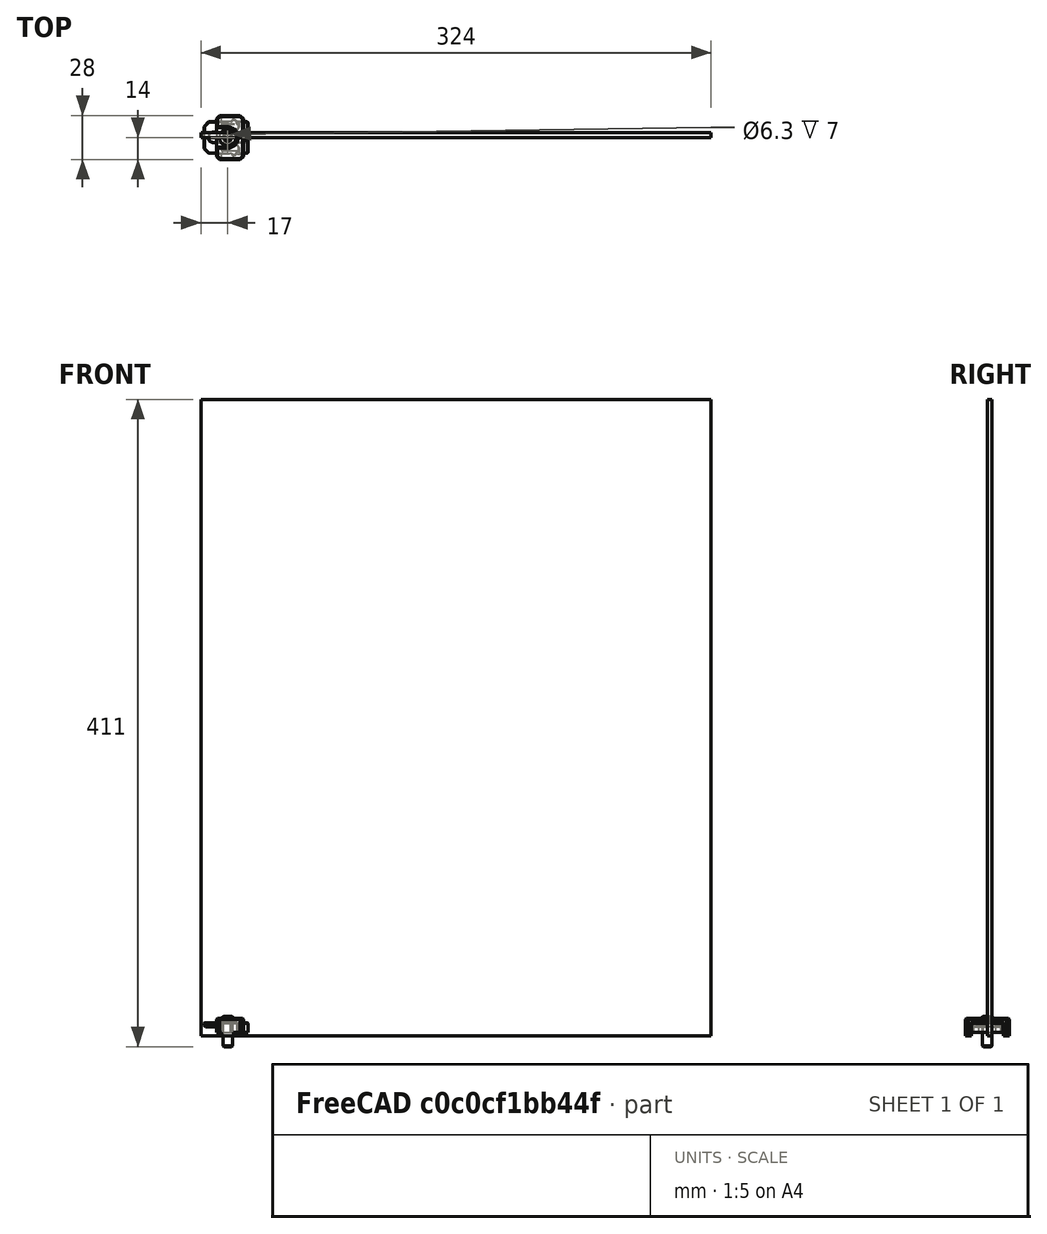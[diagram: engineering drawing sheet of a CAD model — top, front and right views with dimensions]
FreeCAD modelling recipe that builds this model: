
FCSTD DOCUMENT  (FreeCAD 0.19R24291 (Git))
Label: side-panell-assembly
License: Other
LicenseURL: GPL3
objects: Part::Feature×24, App::Part×13, Part::FeaturePython×12, Part::Box×1
note: 37 computed .brp shape members not serialized (recipe doc carries the construction recipe); baked Part::Feature solids carry a one-line shape summary decoded from their .brp

FEATURE [Part::Box] Box  label="panel-324x404x3mm"
  AttacherType = Attacher::AttachEngine3D
  Height = 404
  Length = 324
  Placement = pos=(-2,0,-2) rot=(0,0,1;0rad)
  Width = 3
FEATURE [Part::Feature] Chamfer008001013
  shape: bbox 28 x 22 x 6 mm, 82 faces (baked)
FEATURE [Part::Feature] Chamfer008002001001
  shape: bbox 17 x 28 x 11 mm, 53 faces (baked)
FEATURE [Part::FeaturePython] Screw  label="M6x16-Screw"  # Fasteners workbench fastener (typed FeaturePython)
  Placement = pos=(15,0,7) rot=(0,0,1;0rad)
  baseObject = -> Chamfer008002001001 [Edge135]
  diameter = 4
  invert = false
  length = 3
  lengthCustom = 16
  matchOuter = false
  offset = 0
  thread = false
  type = 40
FEATURE [App::Part] Part013  label="Panel-mounterr2-000"
  Group = -> [Chamfer008001013,Chamfer008002001001,Screw]
  Origin = -> Origin013
  Placement = pos=(39,3,5) rot=(-0.57735,-0.57735,0.57735;4.18879rad)
FEATURE [Part::Feature] Chamfer008002001002
  shape: bbox 28 x 22 x 6 mm, 82 faces (baked)
FEATURE [Part::Feature] Chamfer008002001003
  shape: bbox 17 x 28 x 11 mm, 53 faces (baked)
FEATURE [Part::FeaturePython] Screw024  label="M6x16-Screw001"  # Fasteners workbench fastener (typed FeaturePython)
  Placement = pos=(15,0,7) rot=(0,0,1;0rad)
  baseObject = -> Chamfer008002001003 [Edge135]
  diameter = 4
  invert = false
  length = 3
  lengthCustom = 16
  matchOuter = false
  offset = 0
  thread = false
  type = 40
FEATURE [App::Part] Part014  label="Panel-mounterr2-001"
  Group = -> [Chamfer008002001002,Chamfer008002001003,Screw024]
  Origin = -> Origin014
  Placement = pos=(160,3,5) rot=(-0.57735,-0.57735,0.57735;4.18879rad)
FEATURE [Part::Feature] Chamfer008002001004
  shape: bbox 28 x 22 x 6 mm, 82 faces (baked)
FEATURE [Part::Feature] Chamfer008002001005
  shape: bbox 17 x 28 x 11 mm, 53 faces (baked)
FEATURE [Part::FeaturePython] Screw025  label="M6x16-Screw002"  # Fasteners workbench fastener (typed FeaturePython)
  Placement = pos=(15,0,7) rot=(0,0,1;0rad)
  baseObject = -> Chamfer008002001005 [Edge135]
  diameter = 4
  invert = false
  length = 3
  lengthCustom = 16
  matchOuter = false
  offset = 0
  thread = false
  type = 40
FEATURE [App::Part] Part015  label="Panel-mounterr2-002"
  Group = -> [Chamfer008002001004,Chamfer008002001005,Screw025]
  Origin = -> Origin015
  Placement = pos=(280.5,3,5) rot=(-0.57735,-0.57735,0.57735;4.18879rad)
FEATURE [Part::Feature] Chamfer008002001006
  shape: bbox 28 x 22 x 6 mm, 82 faces (baked)
FEATURE [Part::Feature] Chamfer008002001007
  shape: bbox 17 x 28 x 11 mm, 53 faces (baked)
FEATURE [Part::FeaturePython] Screw026  label="M6x16-Screw003"  # Fasteners workbench fastener (typed FeaturePython)
  Placement = pos=(15,0,7) rot=(0,0,1;0rad)
  baseObject = -> Chamfer008002001007 [Edge135]
  diameter = 4
  invert = false
  length = 3
  lengthCustom = 16
  matchOuter = false
  offset = 0
  thread = false
  type = 40
FEATURE [App::Part] Part016  label="Panel-mounterr2-003"
  Group = -> [Chamfer008002001006,Chamfer008002001007,Screw026]
  Origin = -> Origin016
  Placement = pos=(315,3,39) rot=(-1,0,0;4.71239rad)
FEATURE [Part::Feature] Chamfer008002001008
  shape: bbox 17 x 28 x 11 mm, 53 faces (baked)
FEATURE [Part::FeaturePython] Screw027  label="M6x16-Screw004"  # Fasteners workbench fastener (typed FeaturePython)
  Placement = pos=(15,0,7) rot=(0,0,1;0rad)
  baseObject = -> Chamfer008002001008 [Edge135]
  diameter = 4
  invert = false
  length = 3
  lengthCustom = 16
  matchOuter = false
  offset = 0
  thread = false
  type = 40
FEATURE [Part::Feature] Chamfer008002001009
  shape: bbox 28 x 22 x 6 mm, 82 faces (baked)
FEATURE [App::Part] Part017  label="Panel-mounterr2-004"
  Group = -> [Chamfer008002001009,Chamfer008002001008,Screw027]
  Origin = -> Origin017
  Placement = pos=(315,3,190) rot=(-1,0,0;4.71239rad)
FEATURE [Part::Feature] Chamfer008002001010
  shape: bbox 17 x 28 x 11 mm, 53 faces (baked)
FEATURE [Part::FeaturePython] Screw028  label="M6x16-Screw005"  # Fasteners workbench fastener (typed FeaturePython)
  Placement = pos=(15,0,7) rot=(0,0,1;0rad)
  baseObject = -> Chamfer008002001010 [Edge135]
  diameter = 4
  invert = false
  length = 3
  lengthCustom = 16
  matchOuter = false
  offset = 0
  thread = false
  type = 40
FEATURE [Part::Feature] Chamfer008002001011
  shape: bbox 28 x 22 x 6 mm, 82 faces (baked)
FEATURE [App::Part] Part018  label="Panel-mounterr2-005"
  Group = -> [Chamfer008002001011,Chamfer008002001010,Screw028]
  Origin = -> Origin018
  Placement = pos=(315,3,361) rot=(-1,0,0;4.71239rad)
FEATURE [Part::FeaturePython] Screw029  label="M6x16-Screw006"  # Fasteners workbench fastener (typed FeaturePython)
  Placement = pos=(15,0,7) rot=(0,0,1;0rad)
  baseObject = -> Chamfer008002001012 [Edge135]
  diameter = 4
  invert = false
  length = 3
  lengthCustom = 16
  matchOuter = false
  offset = 0
  thread = false
  type = 40
FEATURE [Part::Feature] Chamfer008002001012
  shape: bbox 17 x 28 x 11 mm, 53 faces (baked)
FEATURE [Part::Feature] Chamfer008002001013
  shape: bbox 28 x 22 x 6 mm, 82 faces (baked)
FEATURE [App::Part] Part019  label="Panel-mounterr2-006"
  Group = -> [Chamfer008002001013,Chamfer008002001012,Screw029]
  Origin = -> Origin019
  Placement = pos=(281,3,395) rot=(-0.57735,0.57735,-0.57735;4.18879rad)
FEATURE [Part::FeaturePython] Screw030  label="M6x16-Screw007"  # Fasteners workbench fastener (typed FeaturePython)
  Placement = pos=(15,0,7) rot=(0,0,1;0rad)
  baseObject = -> Chamfer008002001015 [Edge135]
  diameter = 4
  invert = false
  length = 3
  lengthCustom = 16
  matchOuter = false
  offset = 0
  thread = false
  type = 40
FEATURE [Part::Feature] Chamfer008002001014
  shape: bbox 28 x 22 x 6 mm, 82 faces (baked)
FEATURE [Part::Feature] Chamfer008002001015
  shape: bbox 17 x 28 x 11 mm, 53 faces (baked)
FEATURE [App::Part] Part020  label="Panel-mounterr2-007"
  Group = -> [Chamfer008002001014,Chamfer008002001015,Screw030]
  Origin = -> Origin020
  Placement = pos=(160,3,395) rot=(-0.57735,0.57735,-0.57735;4.18879rad)
FEATURE [Part::FeaturePython] Screw031  label="M6x16-Screw008"  # Fasteners workbench fastener (typed FeaturePython)
  Placement = pos=(15,0,7) rot=(0,0,1;0rad)
  baseObject = -> Chamfer008002001017 [Edge135]
  diameter = 4
  invert = false
  length = 3
  lengthCustom = 16
  matchOuter = false
  offset = 0
  thread = false
  type = 40
FEATURE [Part::Feature] Chamfer008002001016
  shape: bbox 28 x 22 x 6 mm, 82 faces (baked)
FEATURE [Part::Feature] Chamfer008002001017
  shape: bbox 17 x 28 x 11 mm, 53 faces (baked)
FEATURE [App::Part] Part021  label="Panel-mounterr2-008"
  Group = -> [Chamfer008002001016,Chamfer008002001017,Screw031]
  Origin = -> Origin021
  Placement = pos=(5,3,361) rot=(0,0.707107,-0.707107;3.14159rad)
FEATURE [Part::FeaturePython] Screw032  label="M6x16-Screw009"  # Fasteners workbench fastener (typed FeaturePython)
  Placement = pos=(15,0,7) rot=(0,0,1;0rad)
  baseObject = -> Chamfer008002001019 [Edge135]
  diameter = 4
  invert = false
  length = 3
  lengthCustom = 16
  matchOuter = false
  offset = 0
  thread = false
  type = 40
FEATURE [Part::Feature] Chamfer008002001018
  shape: bbox 28 x 22 x 6 mm, 82 faces (baked)
FEATURE [Part::Feature] Chamfer008002001019
  shape: bbox 17 x 28 x 11 mm, 53 faces (baked)
FEATURE [App::Part] Part022  label="Panel-mounterr2-009"
  Group = -> [Chamfer008002001018,Chamfer008002001019,Screw032]
  Origin = -> Origin022
  Placement = pos=(39,3,395) rot=(-0.57735,0.57735,-0.57735;4.18879rad)
FEATURE [Part::Feature] Chamfer008002001020
  shape: bbox 17 x 28 x 11 mm, 53 faces (baked)
FEATURE [Part::Feature] Chamfer008002001021
  shape: bbox 28 x 22 x 6 mm, 82 faces (baked)
FEATURE [Part::FeaturePython] Screw033  label="M6x16-Screw010"  # Fasteners workbench fastener (typed FeaturePython)
  Placement = pos=(15,0,7) rot=(0,0,1;0rad)
  baseObject = -> Chamfer008002001020 [Edge135]
  diameter = 4
  invert = false
  length = 3
  lengthCustom = 16
  matchOuter = false
  offset = 0
  thread = false
  type = 40
FEATURE [App::Part] Part023  label="Panel-mounterr2-010"
  Group = -> [Chamfer008002001021,Chamfer008002001020,Screw033]
  Origin = -> Origin023
  Placement = pos=(5,3,190) rot=(0,0.707107,-0.707107;3.14159rad)
FEATURE [Part::Feature] Chamfer008002001022
  shape: bbox 28 x 22 x 6 mm, 82 faces (baked)
FEATURE [Part::FeaturePython] Screw034  label="M6x16-Screw011"  # Fasteners workbench fastener (typed FeaturePython)
  Placement = pos=(15,0,7) rot=(0,0,1;0rad)
  baseObject = -> Chamfer008002001023 [Edge135]
  diameter = 4
  invert = false
  length = 3
  lengthCustom = 16
  matchOuter = false
  offset = 0
  thread = false
  type = 40
FEATURE [Part::Feature] Chamfer008002001023
  shape: bbox 17 x 28 x 11 mm, 53 faces (baked)
FEATURE [App::Part] Part024  label="Panel-mounterr2-011"
  Group = -> [Chamfer008002001022,Chamfer008002001023,Screw034]
  Origin = -> Origin024
  Placement = pos=(5,3,39) rot=(0,0.707107,-0.707107;3.14159rad)
FEATURE [App::Part] Part  label="side-panel"
  Group = -> [Box,Part013,Part014,Part015,Part016,Part017,Part018,Part019,Part020,Part021,Part022,Part023,Part024]
  Origin = -> Origin
